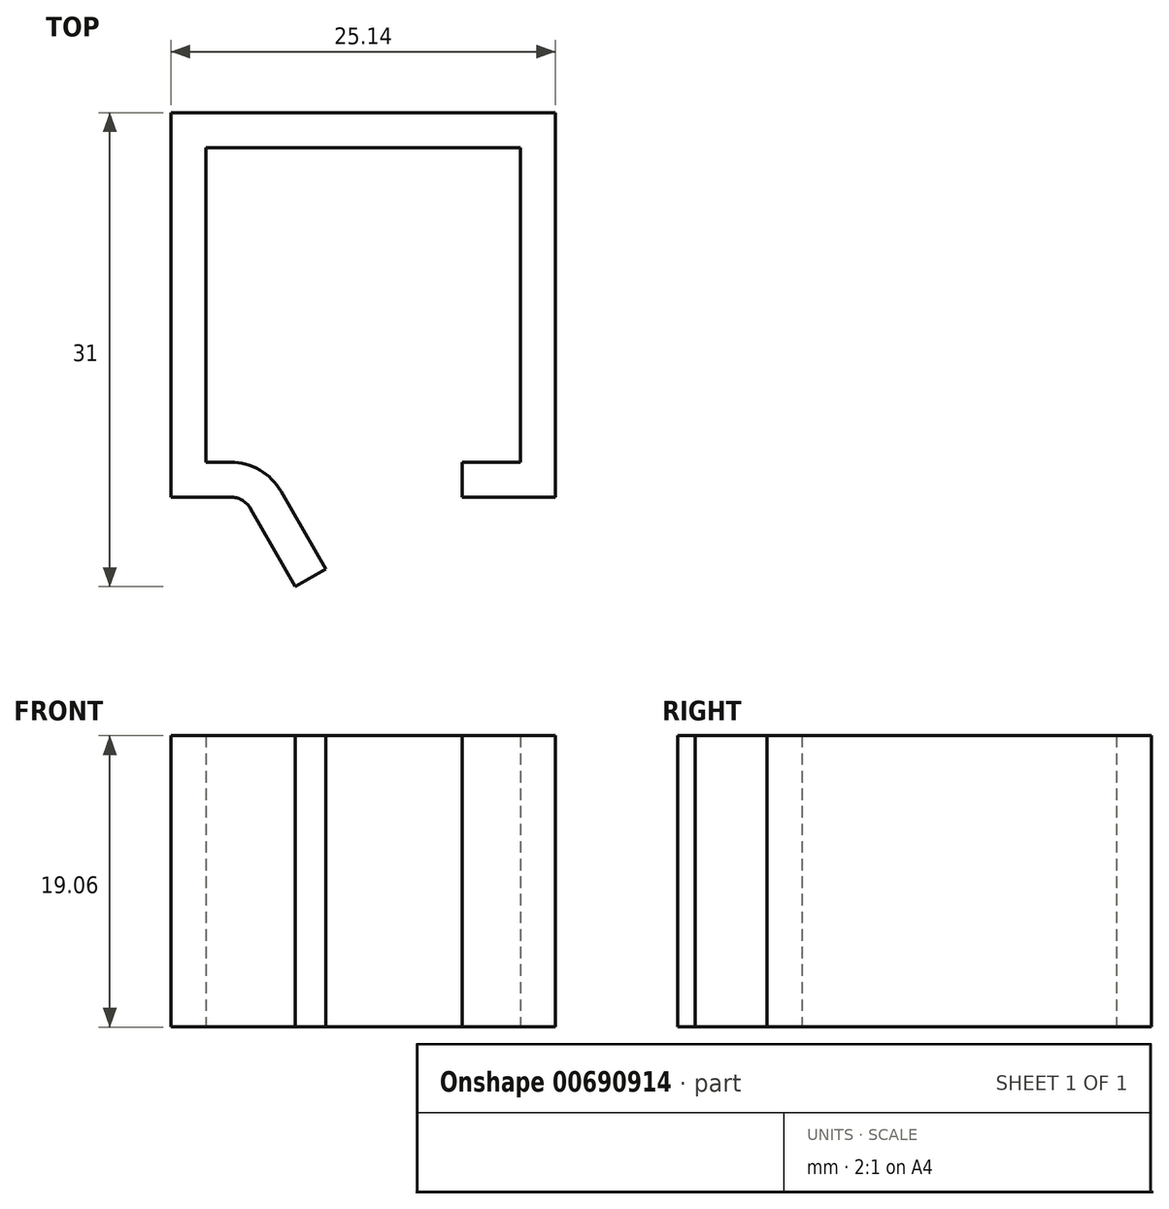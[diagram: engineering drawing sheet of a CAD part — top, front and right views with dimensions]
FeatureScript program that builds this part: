
annotation { "Feature Type Name" : "Feature", "Feature Type Description" : "" }
export const myFeature = defineFeature(function(context is Context, id is Id, definition is map)
    precondition{}
    {
        {
            var Q0;
            Q0=qCreatedBy(makeId("Top.planeOp"),FACE);
            var sketch = newSketch(context, id + "F0", { "sketchPlane" : qUnion([Q0])});
            skLineSegment(sketch, "E0.bottom", {"start": v(10.16, 10.16) * mm, "end": v(-10.16, 10.16) * mm});
            skLineSegment(sketch, "E0.top", {"start": v(10.16, -10.16) * mm, "end": v(-10.16, -10.16) * mm});
            skLineSegment(sketch, "E0.left", {"start": v(10.16, 10.16) * mm, "end": v(10.16, -10.16) * mm});
            skLineSegment(sketch, "E0.right", {"start": v(-10.16, 10.16) * mm, "end": v(-10.16, -10.16) * mm});
            skPoint(sketch, "E0.middle", {"position": v(0, 0) * mm});
            skSolve(sketch);
        }
        {
            var Q0;
            Q0=qCreatedBy(makeId("Top.planeOp"),FACE);
            var sketch = newSketch(context, id + "F1", { "sketchPlane" : qUnion([Q0])});
            skLineSegment(sketch, "E1.0", {"start": v(10.29, -10.29) * mm, "end": v(6.48, -10.29) * mm});
            skLineSegment(sketch, "E1.1", {"start": v(10.29, 10.29) * mm, "end": v(10.29, -10.29) * mm});
            skLineSegment(sketch, "E1.2", {"start": v(10.29, 10.29) * mm, "end": v(-10.29, 10.29) * mm});
            skLineSegment(sketch, "E1.3", {"start": v(-10.29, 10.29) * mm, "end": v(-10.29, -10.29) * mm});
            skLineSegment(sketch, "E2.0", {"start": v(12.57, 12.57) * mm, "end": v(12.57, -12.57) * mm});
            skLineSegment(sketch, "E2.1", {"start": v(12.57, 12.57) * mm, "end": v(-12.57, 12.57) * mm});
            skLineSegment(sketch, "E2.2", {"start": v(-12.57, 12.57) * mm, "end": v(-12.57, -12.57) * mm});
            skLineSegment(sketch, "E2.3", {"start": v(12.57, -12.57) * mm, "end": v(6.48, -12.57) * mm});
            skLineSegment(sketch, "E3", {"start": v(6.48, -10.29) * mm, "end": v(6.48, -12.57) * mm});
            skLineSegment(sketch, "E4", {"start": v(-6.48, -10.29) * mm, "end": v(-2.46, -17.29) * mm});
            skLineSegment(sketch, "E5", {"start": v(-2.46, -17.29) * mm, "end": v(-4.44, -18.43) * mm});
            skLineSegment(sketch, "E6", {"start": v(-4.44, -18.43) * mm, "end": v(-7.8, -12.57) * mm});
            skLineSegment(sketch, "E7.trimOffspring", {"start": v(-6.48, -10.29) * mm, "end": v(-10.29, -10.29) * mm});
            skLineSegment(sketch, "E8.trimOffspring", {"start": v(-7.8, -12.57) * mm, "end": v(-12.57, -12.57) * mm});
            skSolve(sketch);
        }
        {
            var Q0;
            Q0 = qSketchRegion(id + "F1", true);
            extrude(context, id + "F2", {"entities" : qUnion([Q0]), "endBound" : BoundingType.SYMMETRIC, "depth" : 19.05 * mm, "offsetDistance" : 25.4 * mm});
        }
        {
            var Q0;
            Q0=makeQuery(id+"F2.opExtrude","SWEPT_EDGE",EDGE,{"disambiguationData":[OSD([sQuery(id+"F1.wireOp",EDGE,"E4"),sQuery(id+"F1.wireOp",EDGE,"E7.trimOffspring")])]});
            fillet(context, id + "F3", {"entities" : qUnion([Q0]), "radius" : 3.8 * mm, "tangentPropagation" : true, "allowEdgeOverflow" : false});
        }
        {
            var Q0;
            Q0=makeQuery(id+"F2.opExtrude","SWEPT_EDGE",EDGE,{"disambiguationData":[OSD([sQuery(id+"F1.wireOp",EDGE,"E6"),sQuery(id+"F1.wireOp",EDGE,"E8.trimOffspring")])]});
            fillet(context, id + "F4", {"entities" : qUnion([Q0]), "radius" : 1.52 * mm, "tangentPropagation" : true, "allowEdgeOverflow" : false});
        }
    });
